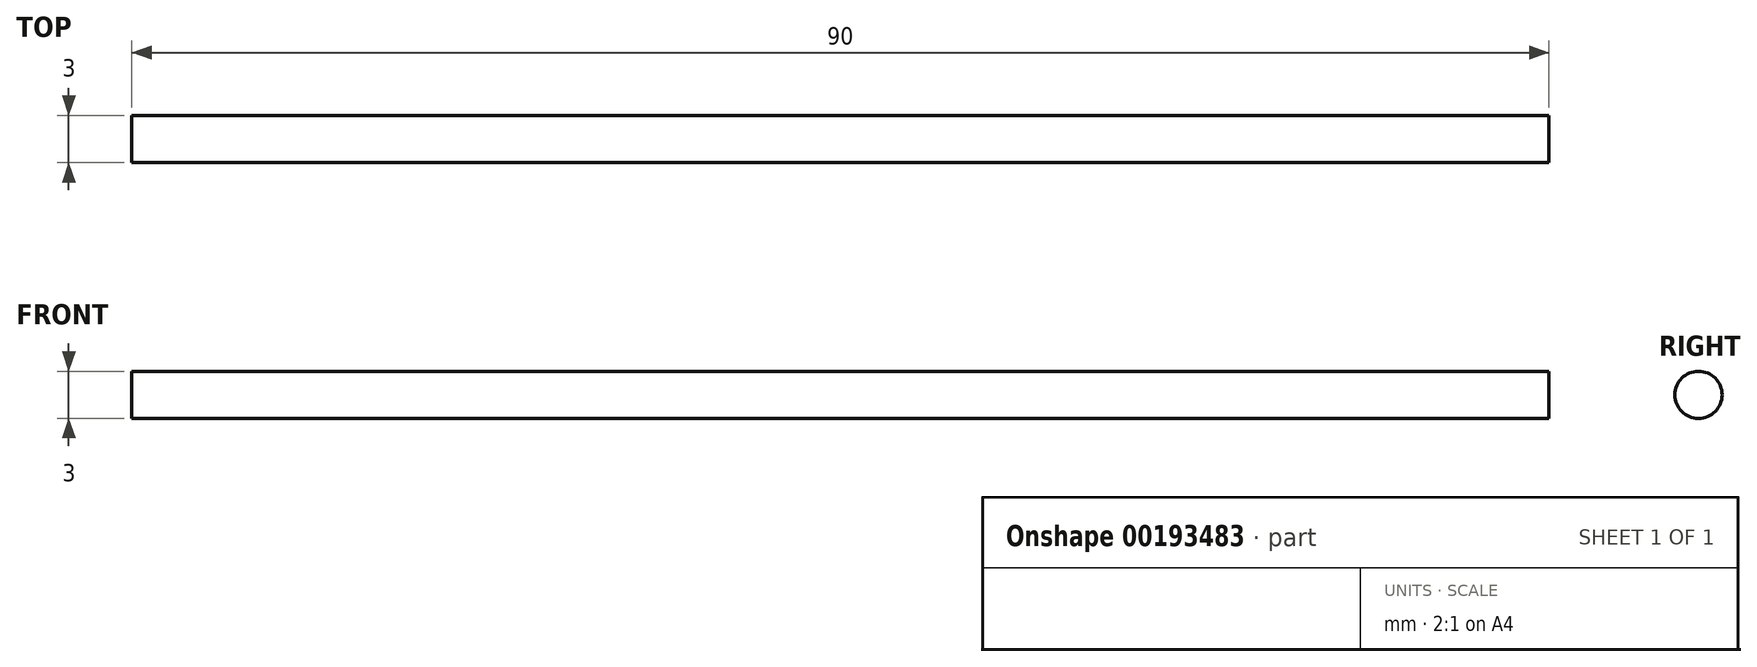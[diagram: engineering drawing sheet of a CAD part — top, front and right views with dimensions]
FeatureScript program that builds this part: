
annotation { "Feature Type Name" : "Feature", "Feature Type Description" : "" }
export const myFeature = defineFeature(function(context is Context, id is Id, definition is map)
    precondition{}
    {
        {
            var Q0;
            Q0=qCreatedBy(makeId("Right.planeOp"),FACE);
            var sketch = newSketch(context, id + "F0", { "sketchPlane" : qUnion([Q0])});
            skCircle(sketch, "E0", {"center": v(0, 0) * mm, "radius": 1.5 * mm});
            skSolve(sketch);
        }
        {
            var Q0;
            Q0 = qSketchRegion(id + "F0", true);
            extrude(context, id + "F1", {"entities" : qUnion([Q0]), "depth" : 90 * mm});
        }
    });
